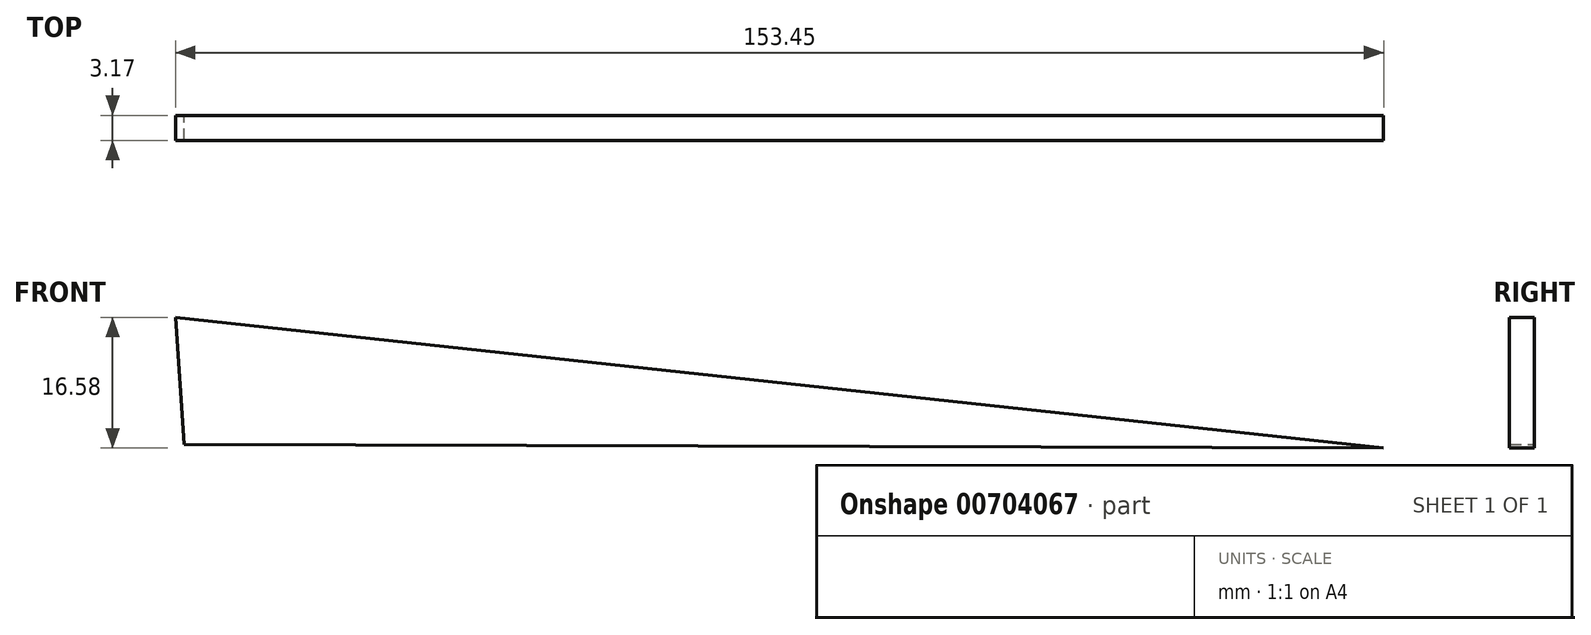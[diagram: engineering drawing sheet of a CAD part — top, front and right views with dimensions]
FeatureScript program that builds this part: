
annotation { "Feature Type Name" : "Feature", "Feature Type Description" : "" }
export const myFeature = defineFeature(function(context is Context, id is Id, definition is map)
    precondition{}
    {
        {
            var Q0;
            Q0=qCreatedBy(makeId("Front.planeOp"),FACE);
            var sketch = newSketch(context, id + "F0", { "sketchPlane" : qUnion([Q0])});
            skLineSegment(sketch, "E0", {"start": v(-64.76, 0.44) * mm, "end": v(87.64, 0) * mm});
            skLineSegment(sketch, "E1", {"start": v(87.64, 0) * mm, "end": v(-65.8, 16.58) * mm});
            skLineSegment(sketch, "E2", {"start": v(-65.8, 16.58) * mm, "end": v(-64.76, 0.44) * mm});
            skSolve(sketch);
        }
        {
            var Q0;
            Q0=makeQuery(id+"F0.imprint","IMPRINT",FACE,{"disambiguationData":[TD([[makeQuery(id+"F0.imprint","IMPRINT",EDGE,{"derivedFrom":sQuery(id+"F0.wireOp",EDGE,"E0")}),1.0]])]});
            extrude(context, id + "F1", {"entities" : qUnion([Q0]), "depth" : 3.17 * mm, "offsetDistance" : 25.4 * mm});
        }
    });
